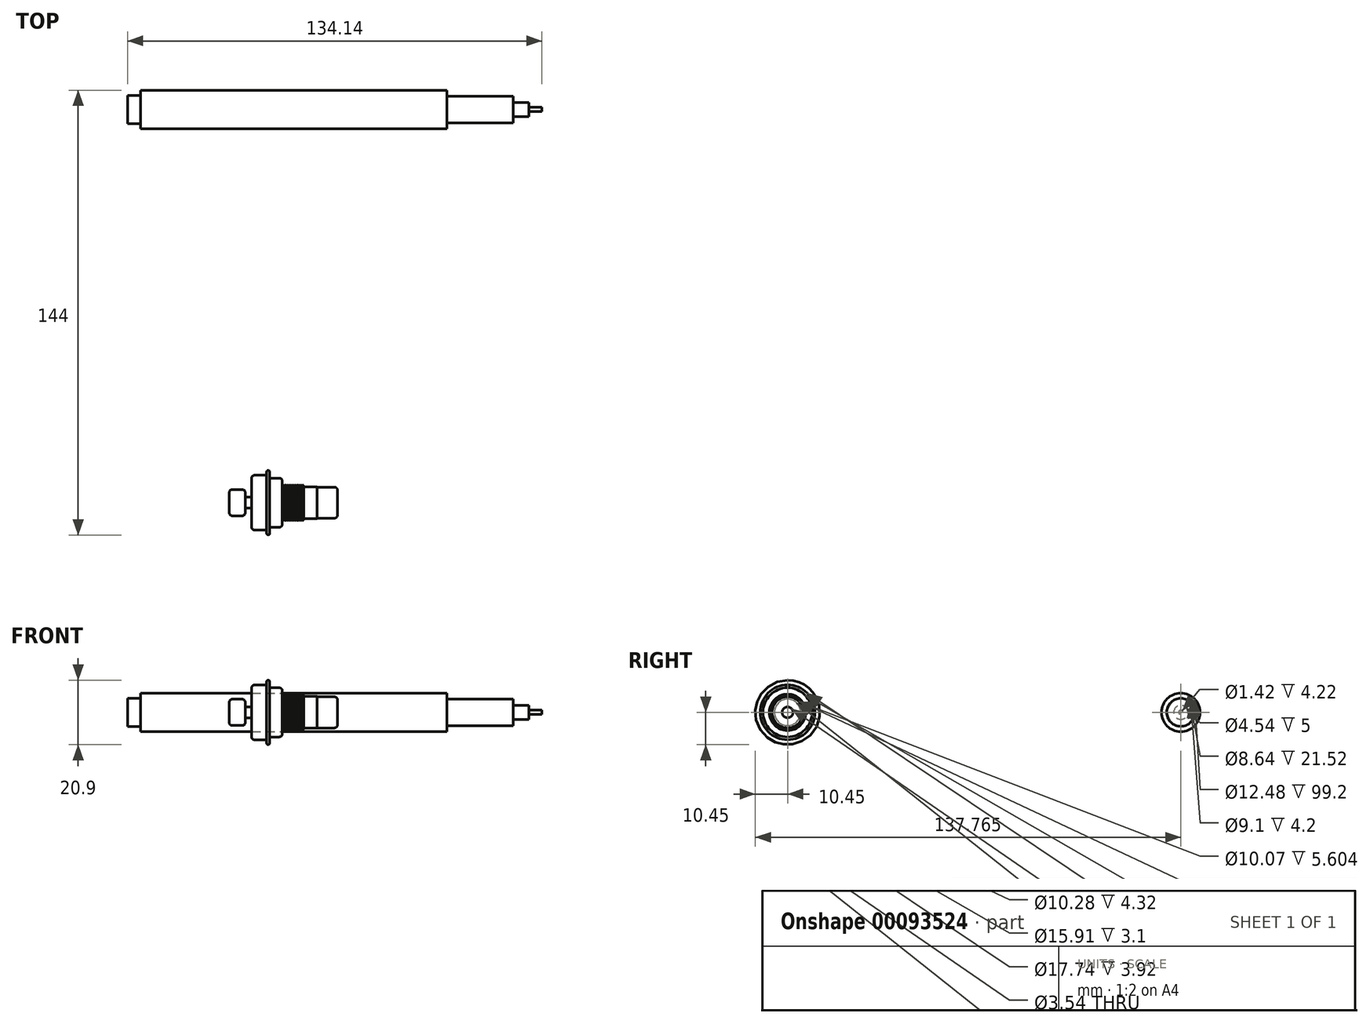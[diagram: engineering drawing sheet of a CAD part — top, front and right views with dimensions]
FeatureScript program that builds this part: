
annotation { "Feature Type Name" : "Feature", "Feature Type Description" : "" }
export const myFeature = defineFeature(function(context is Context, id is Id, definition is map)
    precondition{}
    {
        {
            var Q0;
            Q0=qCreatedBy(makeId("Front.planeOp"),FACE);
            var sketch = newSketch(context, id + "F0", { "sketchPlane" : qUnion([Q0])});
            skLineSegment(sketch, "E0", {"start": v(-22.43, 0) * mm, "end": v(12.31, 0) * mm, "construction": true});
            skLineSegment(sketch, "E1", {"start": v(-22.43, 0) * mm, "end": v(-22.43, 4.26) * mm});
            skLineSegment(sketch, "E2", {"start": v(-22.43, 4.26) * mm, "end": v(-17.24, 4.26) * mm});
            skLineSegment(sketch, "E3", {"start": v(-17.24, 4.26) * mm, "end": v(-17.24, 1.77) * mm});
            skLineSegment(sketch, "E4", {"start": v(-17.24, 1.77) * mm, "end": v(-15.24, 1.77) * mm});
            skLineSegment(sketch, "E5", {"start": v(-15.24, 1.77) * mm, "end": v(-15.24, 8.87) * mm});
            skLineSegment(sketch, "E6", {"start": v(-15.24, 8.87) * mm, "end": v(-10.32, 8.87) * mm});
            skLineSegment(sketch, "E7", {"start": v(-10.32, 8.87) * mm, "end": v(-10.32, 10.45) * mm});
            skLineSegment(sketch, "E8", {"start": v(-10.32, 10.45) * mm, "end": v(-9.32, 10.45) * mm});
            skLineSegment(sketch, "E9", {"start": v(-9.32, 10.45) * mm, "end": v(-9.32, 7.96) * mm});
            skLineSegment(sketch, "E10", {"start": v(-9.32, 7.96) * mm, "end": v(-5.22, 7.96) * mm});
            skLineSegment(sketch, "E11", {"start": v(-5.22, 7.96) * mm, "end": v(-5.22, 5.9) * mm});
            skLineSegment(sketch, "E12", {"start": v(-5.22, 5.9) * mm, "end": v(-5.22, 5.4) * mm});
            skLineSegment(sketch, "E13", {"start": v(-5.22, 5.4) * mm, "end": v(1.7, 5.4) * mm, "construction": true});
            skLineSegment(sketch, "E14", {"start": v(-5.22, 5.9) * mm, "end": v(1.7, 5.9) * mm, "construction": true});
            skLineSegment(sketch, "E15", {"start": v(-5.22, 5.4) * mm, "end": v(-4.22, 5.4) * mm, "construction": true});
            skLineSegment(sketch, "E16", {"start": v(-4.22, 5.4) * mm, "end": v(-3.23, 5.4) * mm, "construction": true});
            skLineSegment(sketch, "E17", {"start": v(-3.23, 5.4) * mm, "end": v(-2.24, 5.4) * mm, "construction": true});
            skLineSegment(sketch, "E18", {"start": v(-2.24, 5.4) * mm, "end": v(-1.25, 5.4) * mm, "construction": true});
            skLineSegment(sketch, "E19", {"start": v(-1.25, 5.4) * mm, "end": v(-0.26, 5.4) * mm, "construction": true});
            skLineSegment(sketch, "E20", {"start": v(1.7, 5.9) * mm, "end": v(0.71, 5.9) * mm, "construction": true});
            skLineSegment(sketch, "E21", {"start": v(0.71, 5.9) * mm, "end": v(-0.28, 5.9) * mm, "construction": true});
            skLineSegment(sketch, "E22.0", {"start": v(0.71, 5.4) * mm, "end": v(-0.28, 5.4) * mm});
            skLineSegment(sketch, "E23.0", {"start": v(1.7, 5.4) * mm, "end": v(0.71, 5.4) * mm});
            skLineSegment(sketch, "E24", {"start": v(-5.22, 5.9) * mm, "end": v(-4.67, 5.9) * mm, "construction": true});
            skLineSegment(sketch, "E25", {"start": v(-3.72, 5.9) * mm, "end": v(-3.72, 5.4) * mm, "construction": true});
            skPoint(sketch, "E25.startSnap0", {"position": v(-3.72, 5.4) * mm});
            skLineSegment(sketch, "E26", {"start": v(-2.73, 5.4) * mm, "end": v(-2.73, 5.9) * mm, "construction": true});
            skLineSegment(sketch, "E27", {"start": v(-1.76, 5.4) * mm, "end": v(-1.76, 5.9) * mm, "construction": true});
            skLineSegment(sketch, "E28", {"start": v(-1.25, 5.4) * mm, "end": v(-0.75, 5.4) * mm, "construction": true});
            skLineSegment(sketch, "E29", {"start": v(-0.75, 5.4) * mm, "end": v(-0.75, 5.9) * mm, "construction": true});
            skLineSegment(sketch, "E30", {"start": v(-0.26, 5.4) * mm, "end": v(0.22, 5.4) * mm, "construction": true});
            skLineSegment(sketch, "E31", {"start": v(0.22, 5.4) * mm, "end": v(0.22, 5.9) * mm, "construction": true});
            skLineSegment(sketch, "E32", {"start": v(1.2, 5.4) * mm, "end": v(1.2, 5.9) * mm, "construction": true});
            skPoint(sketch, "E32.startSnap0", {"position": v(1.2, 5.4) * mm});
            skLineSegment(sketch, "E33", {"start": v(-5.22, 5.4) * mm, "end": v(-4.67, 5.9) * mm});
            skLineSegment(sketch, "E34", {"start": v(-4.67, 5.9) * mm, "end": v(-4.22, 5.4) * mm});
            skLineSegment(sketch, "E35", {"start": v(-4.22, 5.4) * mm, "end": v(-3.72, 5.9) * mm});
            skLineSegment(sketch, "E36", {"start": v(-3.72, 5.9) * mm, "end": v(-3.23, 5.4) * mm});
            skLineSegment(sketch, "E37", {"start": v(-3.23, 5.4) * mm, "end": v(-2.73, 5.9) * mm});
            skLineSegment(sketch, "E38", {"start": v(-2.73, 5.9) * mm, "end": v(-2.24, 5.4) * mm});
            skLineSegment(sketch, "E39", {"start": v(-2.24, 5.4) * mm, "end": v(-1.76, 5.9) * mm});
            skLineSegment(sketch, "E40", {"start": v(-1.76, 5.9) * mm, "end": v(-1.25, 5.4) * mm});
            skLineSegment(sketch, "E41", {"start": v(-1.25, 5.4) * mm, "end": v(-0.75, 5.9) * mm});
            skLineSegment(sketch, "E42", {"start": v(-0.75, 5.9) * mm, "end": v(-0.28, 5.4) * mm});
            skLineSegment(sketch, "E43", {"start": v(-0.28, 5.4) * mm, "end": v(0.22, 5.9) * mm});
            skLineSegment(sketch, "E44", {"start": v(0.22, 5.9) * mm, "end": v(0.71, 5.4) * mm});
            skLineSegment(sketch, "E45", {"start": v(0.71, 5.4) * mm, "end": v(1.2, 5.9) * mm});
            skLineSegment(sketch, "E46", {"start": v(1.2, 5.9) * mm, "end": v(1.7, 5.4) * mm});
            skLineSegment(sketch, "E47", {"start": v(1.7, 5.4) * mm, "end": v(1.7, 5.14) * mm});
            skLineSegment(sketch, "E48", {"start": v(1.7, 5.14) * mm, "end": v(6.02, 5.14) * mm});
            skLineSegment(sketch, "E49", {"start": v(6.02, 5.14) * mm, "end": v(6.02, 5.04) * mm});
            skLineSegment(sketch, "E50", {"start": v(6.02, 5.04) * mm, "end": v(12.63, 5.04) * mm});
            skLineSegment(sketch, "E51", {"start": v(12.63, 0) * mm, "end": v(12.63, 5.04) * mm});
            skLineSegment(sketch, "E52", {"start": v(12.31, 0) * mm, "end": v(12.63, 0) * mm, "construction": true});
            skSolve(sketch);
        }
        {
            var Q0;
            Q0=sQuery(id+"F0.wireOp",EDGE,"E1");
            var Q1;
            Q1=sQuery(id+"F0.wireOp",EDGE,"E2");
            var Q2;
            Q2=sQuery(id+"F0.wireOp",EDGE,"E3");
            var Q3;
            Q3=sQuery(id+"F0.wireOp",EDGE,"E4");
            var Q4;
            Q4=sQuery(id+"F0.wireOp",EDGE,"E5");
            var Q5;
            Q5=sQuery(id+"F0.wireOp",EDGE,"E6");
            var Q6;
            Q6=sQuery(id+"F0.wireOp",EDGE,"E7");
            var Q7;
            Q7=sQuery(id+"F0.wireOp",EDGE,"E8");
            var Q8;
            Q8=sQuery(id+"F0.wireOp",EDGE,"E9");
            var Q9;
            Q9=sQuery(id+"F0.wireOp",EDGE,"E10");
            var Q10;
            Q10=sQuery(id+"F0.wireOp",EDGE,"E12");
            var Q11;
            Q11=sQuery(id+"F0.wireOp",EDGE,"E11");
            var Q12;
            Q12=sQuery(id+"F0.wireOp",EDGE,"E33");
            var Q13;
            Q13=sQuery(id+"F0.wireOp",EDGE,"E34");
            var Q14;
            Q14=sQuery(id+"F0.wireOp",EDGE,"E35");
            var Q15;
            Q15=sQuery(id+"F0.wireOp",EDGE,"E36");
            var Q16;
            Q16=sQuery(id+"F0.wireOp",EDGE,"E37");
            var Q17;
            Q17=sQuery(id+"F0.wireOp",EDGE,"E38");
            var Q18;
            Q18=sQuery(id+"F0.wireOp",EDGE,"E39");
            var Q19;
            Q19=sQuery(id+"F0.wireOp",EDGE,"E40");
            var Q20;
            Q20=sQuery(id+"F0.wireOp",EDGE,"E41");
            var Q21;
            Q21=sQuery(id+"F0.wireOp",EDGE,"E42");
            var Q22;
            Q22=sQuery(id+"F0.wireOp",EDGE,"E43");
            var Q23;
            Q23=sQuery(id+"F0.wireOp",EDGE,"E44");
            var Q24;
            Q24=sQuery(id+"F0.wireOp",EDGE,"E45");
            var Q25;
            Q25=sQuery(id+"F0.wireOp",EDGE,"E46");
            var Q26;
            Q26=sQuery(id+"F0.wireOp",EDGE,"E47");
            var Q27;
            Q27=sQuery(id+"F0.wireOp",EDGE,"E48");
            var Q28;
            Q28=sQuery(id+"F0.wireOp",EDGE,"E49");
            var Q29;
            Q29=sQuery(id+"F0.wireOp",EDGE,"E50");
            var Q30;
            Q30=sQuery(id+"F0.wireOp",EDGE,"E51");
            var Q31;
            Q31=sQuery(id+"F0.wireOp",EDGE,"E0");
            revolve(context, id + "F1", {"bodyType" : ToolBodyType.SURFACE, "surfaceEntities" : qUnion([Q0, Q1, Q2, Q3, Q4, Q5, Q6, Q7, Q8, Q9, Q10, Q11, Q12, Q13, Q14, Q15, Q16, Q17, Q18, Q19, Q20, Q21, Q22, Q23, Q24, Q25, Q26, Q27, Q28, Q29, Q30]), "axis" : qUnion([Q31]), "revolveType" : RevolveType.FULL});
        }
        {
            var Q0;
            Q0=makeQuery(id+"F1.opRevolve","SWEPT_EDGE",EDGE,{"disambiguationData":[OSD([sQuery(id+"F0.wireOp",VERTEX,"E2.start")])]});
            var Q1;
            Q1=makeQuery(id+"F1.opRevolve","SWEPT_EDGE",EDGE,{"disambiguationData":[OSD([sQuery(id+"F0.wireOp",VERTEX,"E3.start")])]});
            var Q2;
            Q2=makeQuery(id+"F1.opRevolve","SWEPT_EDGE",EDGE,{"disambiguationData":[OSD([sQuery(id+"F0.wireOp",VERTEX,"E6.start")])]});
            var Q3;
            Q3=makeQuery(id+"F1.opRevolve","SWEPT_EDGE",EDGE,{"disambiguationData":[OSD([sQuery(id+"F0.wireOp",VERTEX,"E11.start")])]});
            var Q4;
            Q4=makeQuery(id+"F1.opRevolve","SWEPT_EDGE",EDGE,{"disambiguationData":[OSD([sQuery(id+"F0.wireOp",VERTEX,"E51.end")])]});
            fillet(context, id + "F2", {"entities" : qUnion([Q0, Q1, Q2, Q3, Q4]), "radius" : 1 * mm, "tangentPropagation" : true, "allowEdgeOverflow" : false});
        }
        {
            var Q0;
            Q0=makeQuery(id+"F1.opRevolve","SWEPT_EDGE",EDGE,{"disambiguationData":[OSD([sQuery(id+"F0.wireOp",VERTEX,"E9.start")])]});
            var Q1;
            Q1=makeQuery(id+"F1.opRevolve","SWEPT_EDGE",EDGE,{"disambiguationData":[OSD([sQuery(id+"F0.wireOp",VERTEX,"E8.start")])]});
            fillet(context, id + "F3", {"entities" : qUnion([Q0, Q1]), "radius" : 0.5 * mm, "tangentPropagation" : true, "allowEdgeOverflow" : false});
        }
        {
            var Q0;
            Q0=qCreatedBy(makeId("Top.planeOp"),FACE);
            var sketch = newSketch(context, id + "F4", { "sketchPlane" : qUnion([Q0])});
            skLineSegment(sketch, "E53", {"start": v(-55.35, 127.31) * mm, "end": v(78.79, 127.31) * mm, "construction": true});
            skLineSegment(sketch, "E54", {"start": v(-55.35, 127.31) * mm, "end": v(-55.35, 131.86) * mm});
            skLineSegment(sketch, "E55", {"start": v(-55.35, 131.86) * mm, "end": v(-51.15, 131.86) * mm});
            skLineSegment(sketch, "E56", {"start": v(-51.15, 131.86) * mm, "end": v(-51.15, 133.55) * mm});
            skLineSegment(sketch, "E57", {"start": v(-51.15, 133.55) * mm, "end": v(48.05, 133.55) * mm});
            skLineSegment(sketch, "E58", {"start": v(48.05, 133.55) * mm, "end": v(48.05, 131.63) * mm});
            skLineSegment(sketch, "E59", {"start": v(48.05, 131.63) * mm, "end": v(69.57, 131.63) * mm});
            skLineSegment(sketch, "E60", {"start": v(69.57, 127.31) * mm, "end": v(69.57, 129.58) * mm, "construction": true});
            skLineSegment(sketch, "E61", {"start": v(69.57, 131.63) * mm, "end": v(69.57, 129.58) * mm});
            skLineSegment(sketch, "E62", {"start": v(69.57, 129.58) * mm, "end": v(74.57, 129.58) * mm});
            skLineSegment(sketch, "E63", {"start": v(74.57, 129.58) * mm, "end": v(74.57, 128.02) * mm});
            skLineSegment(sketch, "E64", {"start": v(74.57, 128.02) * mm, "end": v(78.79, 128.02) * mm});
            skLineSegment(sketch, "E65", {"start": v(78.79, 128.02) * mm, "end": v(78.79, 127.31) * mm});
            skLineSegment(sketch, "E66", {"start": v(74.57, 128.02) * mm, "end": v(74.57, 127.31) * mm});
            skSolve(sketch);
        }
        {
            var Q0;
            Q0=sQuery(id+"F4.wireOp",EDGE,"E54");
            var Q1;
            Q1=sQuery(id+"F4.wireOp",EDGE,"E55");
            var Q2;
            Q2=sQuery(id+"F4.wireOp",EDGE,"E56");
            var Q3;
            Q3=sQuery(id+"F4.wireOp",EDGE,"E57");
            var Q4;
            Q4=sQuery(id+"F4.wireOp",EDGE,"E58");
            var Q5;
            Q5=sQuery(id+"F4.wireOp",EDGE,"E59");
            var Q6;
            Q6=sQuery(id+"F4.wireOp",EDGE,"E61");
            var Q7;
            Q7=sQuery(id+"F4.wireOp",EDGE,"E62");
            var Q8;
            Q8=sQuery(id+"F4.wireOp",EDGE,"E63");
            var Q9;
            Q9=sQuery(id+"F4.wireOp",EDGE,"E64");
            var Q10;
            Q10=sQuery(id+"F4.wireOp",EDGE,"E65");
            var Q11;
            Q11=sQuery(id+"F4.wireOp",EDGE,"E53");
            revolve(context, id + "F5", {"bodyType" : ToolBodyType.SURFACE, "surfaceEntities" : qUnion([Q0, Q1, Q2, Q3, Q4, Q5, Q6, Q7, Q8, Q9, Q10]), "axis" : qUnion([Q11]), "revolveType" : RevolveType.FULL});
        }
    });
